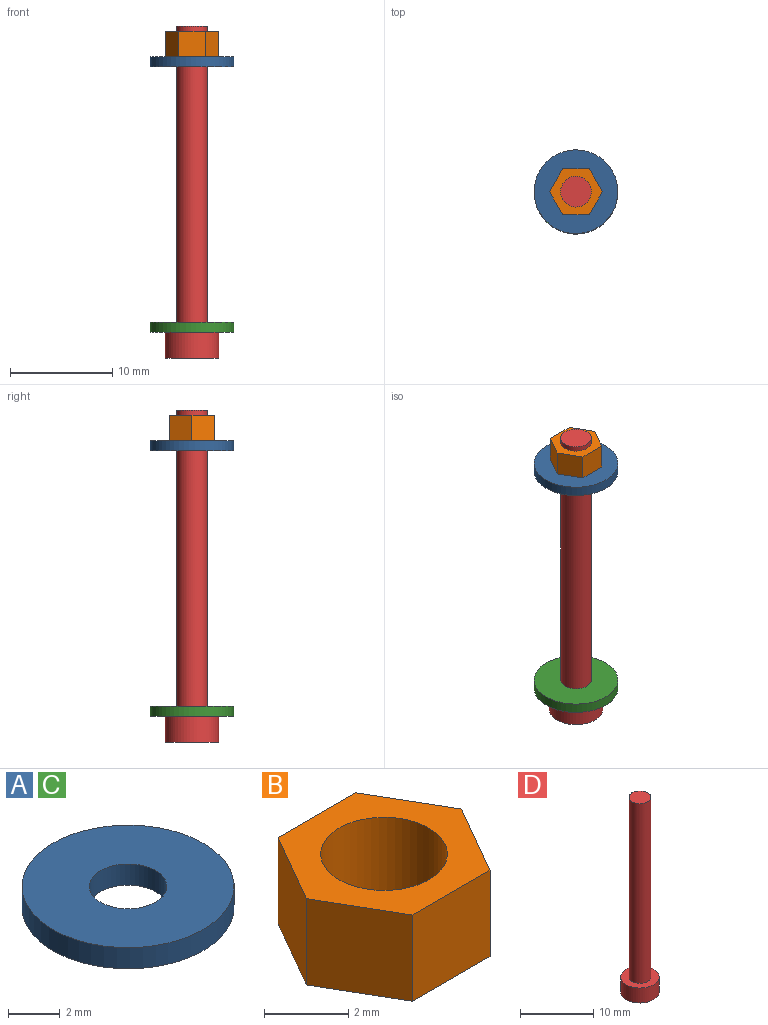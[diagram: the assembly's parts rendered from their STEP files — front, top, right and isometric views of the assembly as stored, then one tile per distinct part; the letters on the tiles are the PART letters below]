
ASSEMBLY  parts=4 mates=3
PART A: 4 faces, bbox 8.2x8.2x1 mm
  f0: cylinder r=1.5mm len=3mm, axis (0,0,-1), area 9.4mm2, adj f2,f3
  f1: cylinder r=4.1mm len=8.2mm, axis (0,0,-1), area 25.8mm2, adj f2,f3
  f2: plane 8.2x8.2mm, normal (0,0,1), area 45.7mm2, adj f0,f1
  f3: plane 8.2x8.2mm, normal (0,0,-1), area 45.7mm2, adj f0,f1
PART B: 9 faces, bbox 5.2x4.5x2.5 mm
  f0: plane 2.6x2.5mm, normal (0,-1,0), area 6.5mm2, adj f1,f5,f7,f8
  f1: plane 2.5x2.25mm, normal (0.87,-0.5,0), area 6.5mm2, adj f0,f2,f7,f8
  f2: plane 2.5x2.25mm, normal (0.87,0.5,0), area 6.5mm2, adj f1,f3,f7,f8
  f3: plane 2.6x2.5mm, normal (0,1,0), area 6.5mm2, adj f2,f4,f7,f8
  f4: plane 2.5x2.25mm, normal (-0.87,0.5,0), area 6.5mm2, adj f3,f5,f7,f8
  f5: plane 2.5x2.25mm, normal (-0.87,-0.5,0), area 6.5mm2, adj f0,f4,f7,f8
  f6: cylinder r=1.5mm len=3mm, axis (0,0,-1), area 23.6mm2, adj f7,f8
  f7: plane 5.2x4.5mm, normal (0,0,1), area 10.5mm2, adj f0,f1,f2,f3,f4,f5,f6
  f8: plane 5.2x4.5mm, normal (0,0,-1), area 10.5mm2, adj f0,f1,f2,f3,f4,f5,f6
PART C: same geometry as A
PART D: 12 faces, bbox 5.3x5.3x32.5 mm
  f0: plane 1.5x1.25mm, normal (-0.87,0.5,0), area 2.2mm2, adj f1,f5,f7,f9
  f1: plane 1.73x1.25mm, normal (0,1,0), area 2.2mm2, adj f0,f2,f7,f9
  f2: plane 1.5x1.25mm, normal (0.87,0.5,0), area 2.2mm2, adj f1,f3,f7,f9
  f3: plane 1.5x1.25mm, normal (0.87,-0.5,0), area 2.2mm2, adj f2,f4,f7,f9
  f4: plane 1.73x1.25mm, normal (0,-1,0), area 2.2mm2, adj f3,f5,f7,f9
  f5: plane 1.5x1.25mm, normal (-0.87,-0.5,0), area 2.2mm2, adj f0,f4,f7,f9
  f6: cylinder r=2.62mm len=5.25mm, axis (0,0,1), area 41.2mm2, adj f7,f8
  f7: plane 5.25x5.25mm, normal (0,0,-1), area 13.9mm2, adj f0,f1,f2,f3,f4,f5,f6
  f8: plane 5.25x5.25mm, normal (0,0,1), area 14.6mm2, adj f6,f10
  f9: plane 3.46x3mm, normal (0,0,-1), area 7.8mm2, adj f0,f1,f2,f3,f4,f5
  f10: cylinder r=1.5mm len=30mm, axis (0,0,-1), area 282.7mm2, adj f8,f11
  f11: plane 3x3mm, normal (0,0,1), area 7.1mm2, adj f10
PLACE A t=(4.96,56.69,91.82)mm
PLACE B rot(axis=(1,0,0),180deg) t=(4.96,16.19,95.32)mm
PLACE C rot(axis=(1,0,0),180deg) t=(4.96,2.69,66.82)mm
PLACE D t=(4.96,16.19,65.82)mm
MATE fastened C.f0 <-> D.f10  axis (0,0,-1) through (4.96,29.69,65.82)mm
MATE fastened A.f0 <-> B.f6  axis (0,0,1) through (4.96,29.69,92.82)mm
MATE fastened A.f0 <-> C.f0  axis (0,0,-1) through (4.96,29.69,91.82)mm
